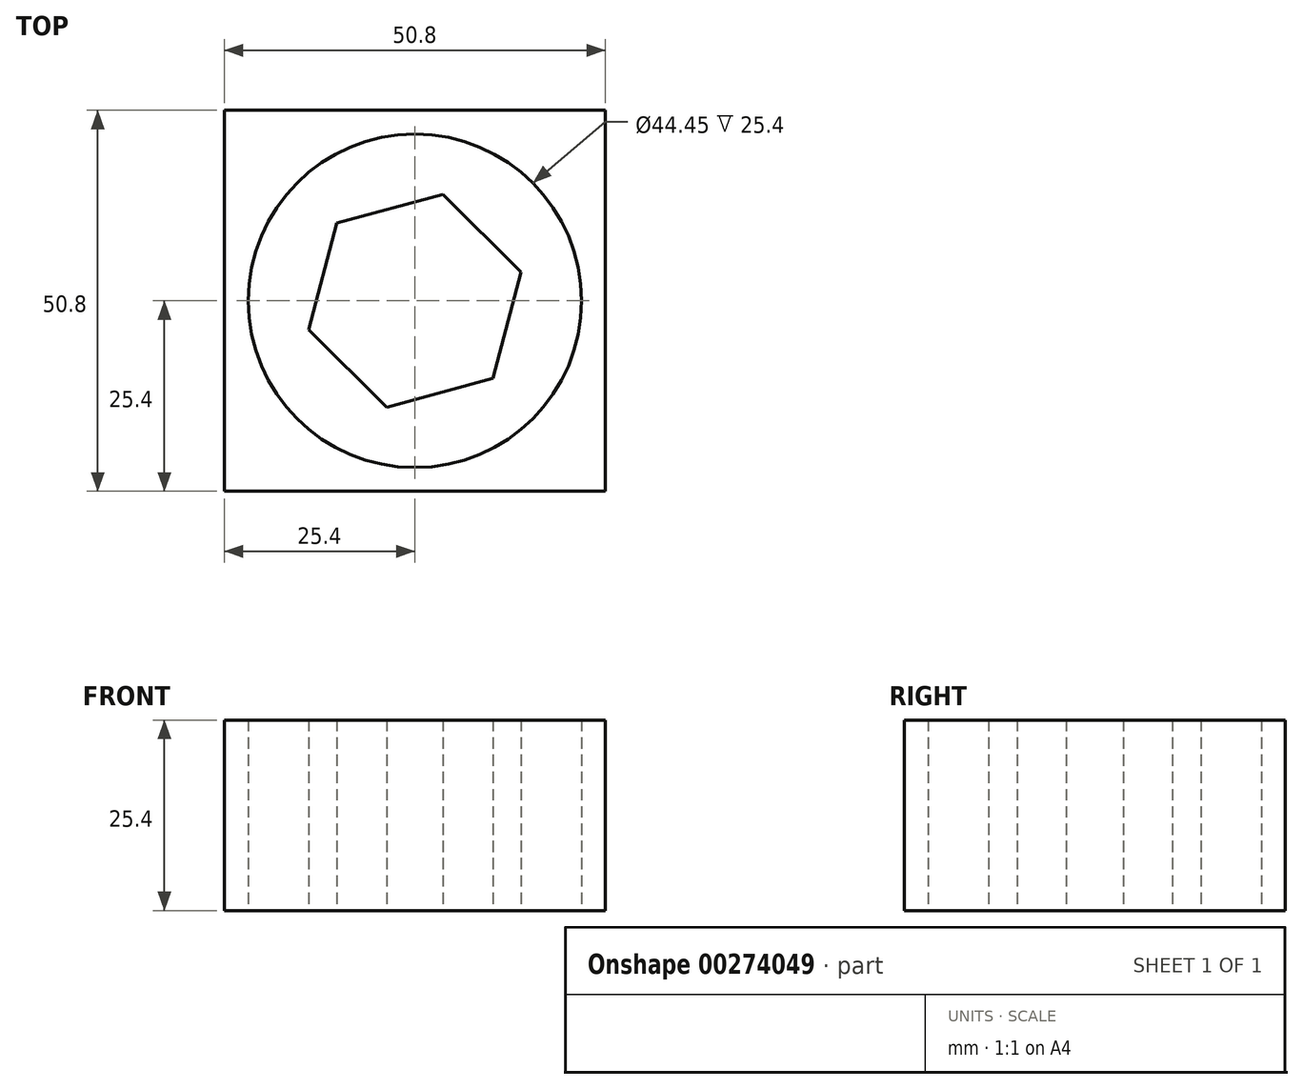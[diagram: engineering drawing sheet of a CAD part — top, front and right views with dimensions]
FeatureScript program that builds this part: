
annotation { "Feature Type Name" : "Feature", "Feature Type Description" : "" }
export const myFeature = defineFeature(function(context is Context, id is Id, definition is map)
    precondition{}
    {
        {
            var Q0;
            Q0=qCreatedBy(makeId("Top.planeOp"),FACE);
            var sketch = newSketch(context, id + "F0", { "sketchPlane" : qUnion([Q0])});
            skLineSegment(sketch, "E0.bottom", {"start": v(25.4, 25.4) * mm, "end": v(-25.4, 25.4) * mm});
            skLineSegment(sketch, "E0.top", {"start": v(25.4, -25.4) * mm, "end": v(-25.4, -25.4) * mm});
            skLineSegment(sketch, "E0.left", {"start": v(25.4, 25.4) * mm, "end": v(25.4, -25.4) * mm});
            skLineSegment(sketch, "E0.right", {"start": v(-25.4, 25.4) * mm, "end": v(-25.4, -25.4) * mm});
            skPoint(sketch, "E0.middle", {"position": v(0, 0) * mm});
            skCircle(sketch, "E1", {"center": v(0, 0) * mm, "radius": 22.23 * mm});
            skCircle(sketch, "E2.cCircle", {"center": v(0, 0) * mm, "radius": 12.7 * mm, "construction": true});
            skLineSegment(sketch, "E2.0", {"start": v(14.16, 3.82) * mm, "end": v(10.39, -10.35) * mm});
            skLineSegment(sketch, "E2.1", {"start": v(10.39, -10.35) * mm, "end": v(-3.77, -14.17) * mm});
            skLineSegment(sketch, "E2.2", {"start": v(-3.77, -14.17) * mm, "end": v(-14.16, -3.82) * mm});
            skLineSegment(sketch, "E2.3", {"start": v(-14.16, -3.82) * mm, "end": v(-10.39, 10.35) * mm});
            skLineSegment(sketch, "E2.4", {"start": v(-10.39, 10.35) * mm, "end": v(3.77, 14.17) * mm});
            skLineSegment(sketch, "E2.5", {"start": v(3.77, 14.17) * mm, "end": v(14.16, 3.82) * mm});
            skPoint(sketch, "E2.0.midPoint", {"position": v(12.27, -3.27) * mm});
            skSolve(sketch);
        }
        {
            var Q0;
            Q0=makeQuery(id+"F0.imprint","IMPRINT",FACE,{"disambiguationData":[TD([[makeQuery(id+"F0.imprint","IMPRINT",EDGE,{"derivedFrom":sQuery(id+"F0.wireOp",EDGE,"E0.bottom")}),1.0]])]});
            var Q1;
            Q1=makeQuery(id+"F0.imprint","IMPRINT",FACE,{"disambiguationData":[TD([[makeQuery(id+"F0.imprint","IMPRINT",EDGE,{"derivedFrom":sQuery(id+"F0.wireOp",EDGE,"E2.0")}),-1.0]])]});
            extrude(context, id + "F1", {"entities" : qUnion([Q0, Q1]), "depth" : 25.4 * mm});
        }
    });
